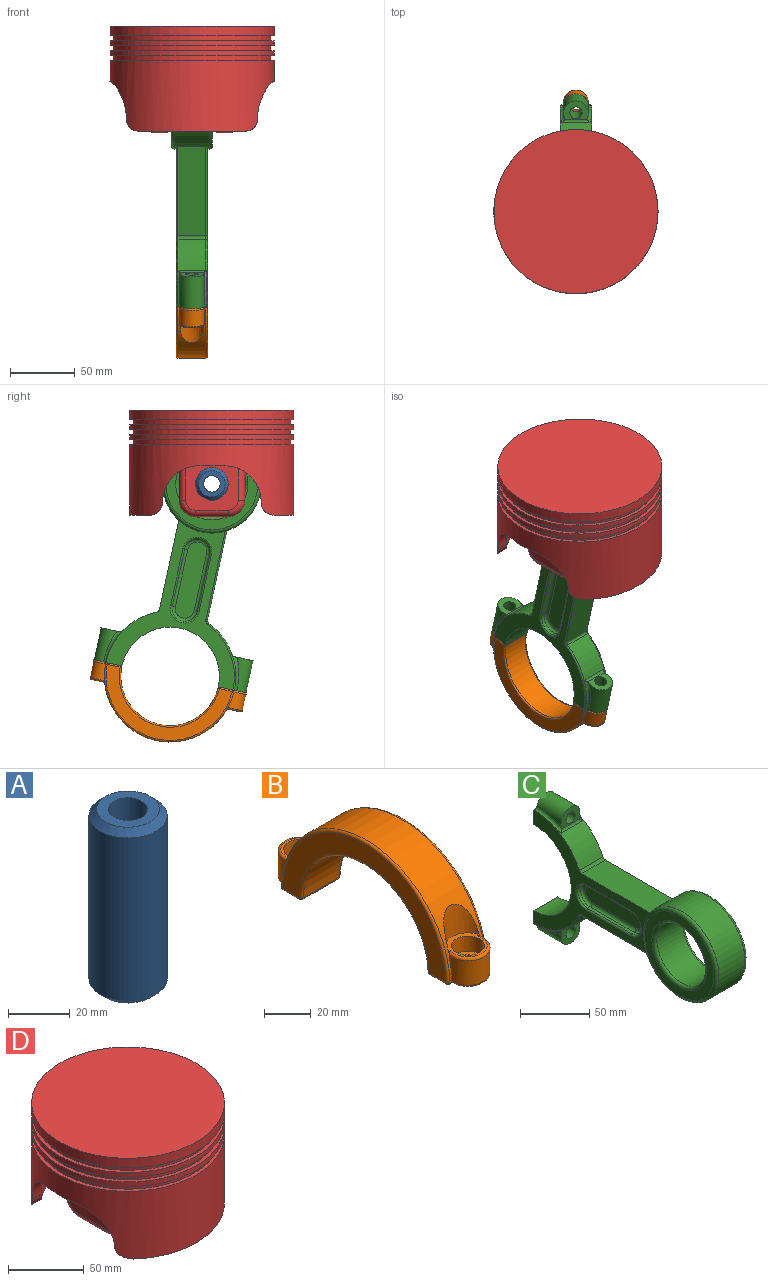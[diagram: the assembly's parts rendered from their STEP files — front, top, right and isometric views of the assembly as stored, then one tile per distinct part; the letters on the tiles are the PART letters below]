
ASSEMBLY  parts=4 mates=5
PART A: 6 faces, bbox 25.4x25.4x69.9 mm
  f0: cylinder r=6.35mm len=69.85mm, axis (0,0,-1), area 2786.9mm2, adj f2,f3
  f1: cylinder r=12.7mm len=64.85mm, axis (0,0,-1), area 5174.8mm2, adj f4,f5
  f2: plane 20.4x20.4mm, normal (0,0,1), area 200.2mm2, adj f0,f5
  f3: plane 20.4x20.4mm, normal (0,0,-1), area 200.2mm2, adj f0,f4
  f4: cone r=12.7mm half-angle=45deg, axis (0,0,1), area 254.4mm2, adj f1,f3
  f5: cone r=10.2mm half-angle=45deg, axis (0,0,-1), area 254.4mm2, adj f1,f2
PART B: 46 faces, bbox 24.1x122.2x55 mm
  f0: cylinder r=50.8mm len=101.57mm, axis (-1,0,0), area 2320.8mm2, adj f6,f7,f8,f12,f13,f14,f21,f29
  f1: plane 21.63x19.75mm, normal (0,0,-1), area 245.3mm2, adj f20,f21,f22,f25,f30,f31,f44
  f2: cylinder r=38.1mm len=76.16mm, axis (-1,0,0), area 2536.6mm2, adj f22,f23,f32,f33
  f3: plane 21.63x19.75mm, normal (0,0,-1), area 245.3mm2, adj f18,f28,f33,f37,f39,f40,f42
  f4: plane 99.07x48.3mm, normal (1,0,0), area 1398.9mm2, adj f20,f23,f28,f29
  f5: plane 99.07x48.3mm, normal (-1,0,0), area 1398.9mm2, adj f31,f32,f38,f39
  f6: plane 18.46x17.8mm, normal (0,0,1), area 84.7mm2, adj f0,f8,f11,f45
  f7: cylinder r=9.53mm len=19.05mm, axis (0,0,-1), area 399.8mm2, adj f0,f21,f25,f30,f45
  f8: cone r=9.53mm half-angle=4deg, axis (0,0,1), area 290.7mm2, adj f0,f6
  f9: cylinder r=4.5mm len=9mm, axis (0,0,1), area 169.6mm2, adj f10,f44
  f10: plane 14.25x14.25mm, normal (0,0,1), area 95.9mm2, adj f9,f11
  f11: cylinder r=7.12mm len=14.25mm, axis (0,0,1), area 358.1mm2, adj f6,f10
  f12: plane 18.46x17.8mm, normal (0,0,1), area 84.7mm2, adj f0,f14,f17,f43
  f13: cylinder r=9.53mm len=19.05mm, axis (0,0,-1), area 399.8mm2, adj f0,f37,f40,f42,f43
  f14: cone r=9.53mm half-angle=4deg, axis (0,0,1), area 290.7mm2, adj f0,f12
  f15: cylinder r=4.5mm len=9mm, axis (0,0,1), area 169.6mm2, adj f16,f18
  f16: plane 14.25x14.25mm, normal (0,0,1), area 95.9mm2, adj f15,f17
  f17: cylinder r=7.12mm len=14.25mm, axis (0,0,1), area 358.1mm2, adj f12,f16
  f18: torus R=5.75mm, axis (0,0,1), area 61.1mm2, adj f3,f15
  f19: sphere r=1.25mm, area 2.4mm2, adj f20,f22,f23
  f20: cylinder r=1.25mm len=10.2mm, axis (0,-1,0), area 20mm2, adj f1,f4,f19,f24
  f21: cylinder r=1.25mm len=2.64mm, axis (-1,0,0), area 3.5mm2, adj f0,f1,f7,f24,f25
  f22: cylinder r=1.25mm len=21.63mm, axis (-1,0,0), area 41.6mm2, adj f1,f2,f19,f26
  f23: torus R=39.35mm, axis (1,0,0), area 233mm2, adj f2,f4,f19,f27
  f24: sphere r=1.25mm, area 2.5mm2, adj f20,f21,f29
  f25: torus R=8.27mm, axis (0,0,1), area 57.8mm2, adj f1,f7,f21,f30
  f26: sphere r=1.25mm, area 2.4mm2, adj f22,f31,f32
  f27: sphere r=1.25mm, area 2.4mm2, adj f23,f28,f33
  f28: cylinder r=1.25mm len=10.2mm, axis (0,-1,0), area 20mm2, adj f3,f4,f27,f34
  f29: torus R=49.55mm, axis (1,0,0), area 305.6mm2, adj f0,f4,f24,f34
  f30: cylinder r=1.25mm len=2.64mm, axis (-1,0,0), area 3.5mm2, adj f0,f1,f7,f25,f35
  f31: cylinder r=1.25mm len=10.2mm, axis (0,1,0), area 20mm2, adj f1,f5,f26,f35
  f32: torus R=39.35mm, axis (1,0,0), area 233mm2, adj f2,f5,f26,f36
  f33: cylinder r=1.25mm len=21.63mm, axis (-1,0,0), area 41.6mm2, adj f2,f3,f27,f36
  f34: sphere r=1.25mm, area 2.5mm2, adj f28,f29,f37
  f35: sphere r=1.25mm, area 2.5mm2, adj f30,f31,f38
  f36: sphere r=1.25mm, area 2.4mm2, adj f32,f33,f39
  f37: cylinder r=1.25mm len=2.64mm, axis (-1,0,0), area 3.5mm2, adj f0,f3,f13,f34,f40
  f38: torus R=49.55mm, axis (1,0,0), area 305.6mm2, adj f0,f5,f35,f41
  f39: cylinder r=1.25mm len=10.2mm, axis (0,1,0), area 20mm2, adj f3,f5,f36,f41
  f40: torus R=8.27mm, axis (0,0,1), area 57.8mm2, adj f3,f13,f37,f42
  f41: sphere r=1.25mm, area 2.5mm2, adj f38,f39,f42
  f42: cylinder r=1.25mm len=2.64mm, axis (-1,0,0), area 3.5mm2, adj f0,f3,f13,f40,f41
  f43: torus R=8.27mm, axis (0,0,-1), area 64.7mm2, adj f0,f12,f13
  f44: torus R=5.75mm, axis (0,0,1), area 61.1mm2, adj f1,f9
  f45: torus R=8.27mm, axis (0,0,-1), area 64.7mm2, adj f0,f6,f7
PART C: 68 faces, bbox 31.9x199x120.8 mm
  f0: cylinder r=50.8mm len=22.73mm, axis (-1,0,0), area 662.3mm2, adj f42,f43,f44,f51,f54,f57
  f1: cylinder r=50.8mm len=15.49mm, axis (-1,0,0), area 2.1mm2, adj f7,f10,f41
  f2: cylinder r=50.8mm len=30.96mm, axis (-1,0,0), area 754.3mm2, adj f9,f10,f39,f40,f41,f49
  f3: cylinder r=50.8mm len=15.49mm, axis (-1,0,0), area 2.1mm2, adj f7,f9,f39
  f4: plane 70.63x21.63mm, normal (0,0,-1), area 1527.7mm2, adj f11,f51,f52,f59
  f5: plane 24.15x22.25mm, normal (0,1,0), area 379.3mm2, adj f6,f9,f10,f16,f17,f42,f43,f55
  f6: cylinder r=38.1mm len=76.2mm, axis (-1,0,0), area 2888.2mm2, adj f5,f7,f9,f10
  f7: plane 24.18x22.28mm, normal (0,1,0), area 379.7mm2, adj f1,f3,f6,f9,f10,f18,f20,f39
  f8: plane 69.19x24.13mm, normal (0,0,1), area 1669.6mm2, adj f9,f10,f49,f50
  f9: plane 120.13x100.48mm, normal (1,0,0), area 2732.6mm2, adj f2,f3,f5,f6,f7,f8,f11,f49
  f10: plane 120.13x100.48mm, normal (-1,0,0), area 2732.6mm2, adj f1,f2,f5,f6,f7,f8,f11,f49
  f11: cylinder r=38.1mm len=76.2mm, axis (-1,0,0), area 5390mm2, adj f4,f9,f10,f46,f48,f50,f52,f59
  f12: cylinder r=25.4mm len=50.8mm, axis (-1,0,0), area 4256.3mm2, adj f45,f47
  f13: plane 71.12x71.12mm, normal (1,0,0), area 1520.1mm2, adj f47,f48
  f14: plane 71.12x71.12mm, normal (-1,0,0), area 1520.1mm2, adj f45,f46
  f15: plane 19.05x14.89mm, normal (0,-1,0), area 169.6mm2, adj f16,f17,f42,f43,f44
  f16: cylinder r=9.53mm len=25.4mm, axis (0,1,0), area 788.3mm2, adj f5,f15,f42,f43
  f17: cylinder r=4.76mm len=25.4mm, axis (0,1,0), area 759.7mm2, adj f5,f15
  f18: cylinder r=9.53mm len=25.4mm, axis (0,1,0), area 788.3mm2, adj f7,f19,f39,f41
  f19: plane 19.17x15.01mm, normal (0,-1,0), area 169.6mm2, adj f18,f20,f39,f40,f41
  f20: cylinder r=4.76mm len=25.4mm, axis (0,1,0), area 759.7mm2, adj f7,f19
  f21: plane 45x2.56mm, normal (0,0,1), area 115.2mm2, adj f22,f24,f35,f64
  f22: cylinder r=10mm len=20mm, axis (1,0,0), area 80.4mm2, adj f21,f23,f36,f65
  f23: plane 45x2.56mm, normal (0,0,-1), area 115.2mm2, adj f22,f24,f38,f67
  f24: cylinder r=10mm len=20mm, axis (1,0,0), area 80.4mm2, adj f21,f23,f37,f66
  f25: plane 59.92x14.92mm, normal (1,0,0), area 846.2mm2, adj f35,f36,f37,f38
  f26: plane 45x2.56mm, normal (0,0,1), area 115.2mm2, adj f27,f29,f31,f63
  f27: cylinder r=10mm len=20mm, axis (-1,0,0), area 80.4mm2, adj f26,f28,f33,f62
  f28: plane 45x2.56mm, normal (0,0,-1), area 115.2mm2, adj f27,f29,f34,f60
  f29: cylinder r=10mm len=20mm, axis (-1,0,0), area 80.4mm2, adj f26,f28,f32,f61
  f30: plane 59.92x14.92mm, normal (-1,0,0), area 846.2mm2, adj f31,f32,f33,f34
  f31: cylinder r=2.54mm len=45mm, axis (0,-1,0), area 179.5mm2, adj f26,f30,f32,f33
  f32: torus R=7.46mm, axis (-1,0,0), area 113.8mm2, adj f29,f30,f31,f34
  f33: torus R=7.46mm, axis (-1,0,0), area 113.8mm2, adj f27,f30,f31,f34
  f34: cylinder r=2.54mm len=45mm, axis (0,1,0), area 179.5mm2, adj f28,f30,f32,f33
  f35: cylinder r=2.54mm len=45mm, axis (0,1,0), area 179.5mm2, adj f21,f25,f36,f37
  f36: torus R=7.46mm, axis (1,0,0), area 113.8mm2, adj f22,f25,f35,f38
  f37: torus R=7.46mm, axis (1,0,0), area 113.8mm2, adj f24,f25,f35,f38
  f38: cylinder r=2.54mm len=45mm, axis (0,-1,0), area 179.5mm2, adj f23,f25,f36,f37
  f39: bspline ~33.55x11.07mm, area 105.2mm2, adj f2,f3,f7,f18,f19,f40
  f40: cylinder r=2.54mm len=21.62mm, axis (-1,0,0), area 51.5mm2, adj f2,f19,f39,f41
  f41: bspline ~31.85x10.39mm, area 105.2mm2, adj f1,f2,f7,f18,f19,f40
  f42: bspline ~32.45x10.36mm, area 85.8mm2, adj f0,f5,f15,f16,f44,f56
  f43: bspline ~31.54x10.2mm, area 85.8mm2, adj f0,f5,f15,f16,f44,f55
  f44: cylinder r=2.54mm len=21.62mm, axis (-1,0,0), area 51.5mm2, adj f0,f15,f42,f43
  f45: torus R=27.94mm, axis (1,0,0), area 659.9mm2, adj f12,f14
  f46: torus R=35.56mm, axis (1,0,0), area 932mm2, adj f11,f14
  f47: torus R=27.94mm, axis (1,0,0), area 659.9mm2, adj f12,f13
  f48: torus R=35.56mm, axis (1,0,0), area 932mm2, adj f11,f13
  f49: cylinder r=2.54mm len=24.13mm, axis (-1,0,0), area 70.7mm2, adj f2,f8,f9,f10
  f50: cylinder r=2.54mm len=24.13mm, axis (-1,0,0), area 61.9mm2, adj f8,f9,f10,f11
  f51: cylinder r=2.54mm len=21.63mm, axis (-1,0,0), area 63.4mm2, adj f0,f4,f53,f58
  f52: cylinder r=1.25mm len=70.63mm, axis (0,1,0), area 138mm2, adj f4,f10,f11,f53
  f53: torus R=3.79mm, axis (1,0,0), area 6.8mm2, adj f10,f51,f52,f54
  f54: torus R=49.55mm, axis (1,0,0), area 59.6mm2, adj f0,f10,f53,f55
  f55: bspline ~32.87x9.3mm, area 45.1mm2, adj f5,f10,f43,f54
  f56: bspline ~31.09x9.09mm, area 45.1mm2, adj f5,f9,f42,f57
  f57: torus R=49.55mm, axis (1,0,0), area 59.6mm2, adj f0,f9,f56,f58
  f58: torus R=3.79mm, axis (1,0,0), area 6.8mm2, adj f9,f51,f57,f59
  f59: cylinder r=1.25mm len=70.63mm, axis (0,-1,0), area 138mm2, adj f4,f9,f11,f58
  f60: cylinder r=1.25mm len=45mm, axis (0,1,0), area 88.4mm2, adj f10,f28,f61,f62
  f61: torus R=11.25mm, axis (1,0,0), area 64.5mm2, adj f10,f29,f60,f63
  f62: torus R=11.25mm, axis (1,0,0), area 64.5mm2, adj f10,f27,f60,f63
  f63: cylinder r=1.25mm len=45mm, axis (0,-1,0), area 88.4mm2, adj f10,f26,f61,f62
  f64: cylinder r=1.25mm len=45mm, axis (0,-1,0), area 88.4mm2, adj f9,f21,f65,f66
  f65: torus R=11.25mm, axis (1,0,0), area 64.5mm2, adj f9,f22,f64,f67
  f66: torus R=11.25mm, axis (1,0,0), area 64.5mm2, adj f9,f24,f64,f67
  f67: cylinder r=1.25mm len=45mm, axis (0,1,0), area 88.4mm2, adj f9,f23,f65,f66
PART D: 68 faces, bbox 127x127x83.5 mm
  f0: plane 114.3x114.3mm, normal (0,0,-1), area 8373.3mm2, adj f12,f28,f29,f30,f31,f33,f34,f35
  f1: plane 82.91x15.4mm, normal (0,0,-1), area 495.6mm2, adj f10,f12,f44,f46
  f2: cylinder r=63.5mm len=127mm, axis (0,0,1), area 1520.1mm2, adj f6,f7
  f3: cylinder r=63.5mm len=127mm, axis (0,0,1), area 1520.1mm2, adj f9,f13
  f4: plane 127x127mm, normal (0,0,1), area 993.1mm2, adj f5,f10
  f5: cylinder r=60.96mm len=121.92mm, axis (0,0,1), area 1459.3mm2, adj f4,f6
  f6: plane 127x127mm, normal (0,0,-1), area 993.1mm2, adj f2,f5
  f7: plane 127x127mm, normal (0,0,1), area 993.1mm2, adj f2,f8
  f8: cylinder r=60.96mm len=121.92mm, axis (0,0,1), area 1459.3mm2, adj f7,f9
  f9: plane 127x127mm, normal (0,0,-1), area 993.1mm2, adj f3,f8
  f10: cylinder r=63.5mm len=127mm, axis (0,0,1), area 16234.2mm2, adj f1,f4,f11,f18,f19,f20,f21,f22
  f11: plane 82.91x15.4mm, normal (0,0,-1), area 495.6mm2, adj f10,f12,f45,f47
  f12: cylinder r=57.15mm len=114.3mm, axis (0,0,-1), area 16707.7mm2, adj f0,f1,f11,f18,f19,f20,f21,f22
  f13: plane 127x127mm, normal (0,0,1), area 993.1mm2, adj f3,f14
  f14: cylinder r=60.96mm len=121.92mm, axis (0,0,1), area 1459.3mm2, adj f13,f15
  f15: plane 127x127mm, normal (0,0,-1), area 993.1mm2, adj f14,f17
  f16: plane 127x127mm, normal (0,0,1), area 12667.7mm2, adj f17
  f17: cylinder r=63.5mm len=127mm, axis (0,0,1), area 3040.2mm2, adj f15,f16
  f18: plane 8.2x0.1mm, normal (0,1,0), area 0.8mm2, adj f10,f12,f27,f47
  f19: plane 20.2x7.25mm, normal (0,0,-1), area 128.9mm2, adj f10,f12,f26,f27
  f20: plane 8.2x0.1mm, normal (0,-1,0), area 0.8mm2, adj f10,f12,f26,f46
  f21: plane 8.2x0.1mm, normal (0,-1,0), area 0.8mm2, adj f10,f12,f24,f44
  f22: plane 20.2x7.25mm, normal (0,0,-1), area 128.9mm2, adj f10,f12,f24,f25
  f23: plane 8.2x0.1mm, normal (0,1,0), area 0.8mm2, adj f10,f12,f25,f45
  f24: cylinder r=28mm len=28mm, axis (-1,0,0), area 322.6mm2, adj f10,f12,f21,f22
  f25: cylinder r=28mm len=28mm, axis (1,0,0), area 322.6mm2, adj f10,f12,f22,f23
  f26: cylinder r=28mm len=28mm, axis (-1,0,0), area 322.6mm2, adj f10,f12,f19,f20
  f27: cylinder r=28mm len=28mm, axis (1,0,0), area 322.6mm2, adj f10,f12,f18,f19
  f28: plane 58.5x40.8mm, normal (-1,0,0), area 1854.6mm2, adj f0,f39,f53,f54,f55,f56,f57
  f29: plane 50.8x9mm, normal (0,1,0), area 457.2mm2, adj f0,f42,f52,f57
  f30: plane 58.5x40.8mm, normal (1,0,0), area 1854.6mm2, adj f0,f39,f48,f49,f50,f51,f52
  f31: plane 50.8x9mm, normal (0,-1,0), area 457.2mm2, adj f0,f43,f48,f53
  f32: plane 25.4x9mm, normal (0,0,-1), area 228.6mm2, adj f42,f43,f50,f55
  f33: plane 58.5x40.8mm, normal (1,0,0), area 1854.6mm2, adj f0,f38,f63,f64,f65,f66,f67
  f34: plane 50.8x9mm, normal (0,-1,0), area 457.2mm2, adj f0,f40,f58,f63
  f35: plane 58.5x40.8mm, normal (-1,0,0), area 1854.6mm2, adj f0,f38,f58,f59,f60,f61,f62
  f36: plane 50.8x9mm, normal (0,1,0), area 457.2mm2, adj f0,f41,f62,f67
  f37: plane 25.4x9mm, normal (0,0,-1), area 228.6mm2, adj f40,f41,f60,f65
  f38: cylinder r=12.7mm len=25.4mm, axis (1,0,0), area 1516.1mm2, adj f33,f35
  f39: cylinder r=12.7mm len=25.4mm, axis (1,0,0), area 1516.1mm2, adj f28,f30
  f40: cylinder r=12.7mm len=12.7mm, axis (1,0,0), area 179.5mm2, adj f34,f37,f59,f64
  f41: cylinder r=12.7mm len=12.7mm, axis (-1,0,0), area 179.5mm2, adj f36,f37,f61,f66
  f42: cylinder r=12.7mm len=12.7mm, axis (-1,0,0), area 179.5mm2, adj f29,f32,f51,f56
  f43: cylinder r=12.7mm len=12.7mm, axis (1,0,0), area 179.5mm2, adj f31,f32,f49,f54
  f44: cylinder r=10mm len=19.94mm, axis (1,0,0), area 140mm2, adj f1,f10,f12,f21
  f45: cylinder r=10mm len=19.94mm, axis (-1,0,0), area 140mm2, adj f10,f11,f12,f23
  f46: cylinder r=10mm len=19.94mm, axis (1,0,0), area 140mm2, adj f1,f10,f12,f20
  f47: cylinder r=10mm len=19.94mm, axis (-1,0,0), area 140mm2, adj f10,f11,f12,f18
  f48: cylinder r=5mm len=50.8mm, axis (0,0,-1), area 399mm2, adj f0,f30,f31,f49
  f49: torus R=7.7mm, axis (-1,0,0), area 134.3mm2, adj f30,f43,f48,f50
  f50: cylinder r=5mm len=25.4mm, axis (0,1,0), area 199.5mm2, adj f30,f32,f49,f51
  f51: torus R=7.7mm, axis (-1,0,0), area 134.3mm2, adj f30,f42,f50,f52
  f52: cylinder r=5mm len=50.8mm, axis (0,0,1), area 399mm2, adj f0,f29,f30,f51
  f53: cylinder r=5mm len=50.8mm, axis (0,0,1), area 399mm2, adj f0,f28,f31,f54
  f54: torus R=7.7mm, axis (-1,0,0), area 134.3mm2, adj f28,f43,f53,f55
  f55: cylinder r=5mm len=25.4mm, axis (0,-1,0), area 199.5mm2, adj f28,f32,f54,f56
  f56: torus R=7.7mm, axis (-1,0,0), area 134.3mm2, adj f28,f42,f55,f57
  f57: cylinder r=5mm len=50.8mm, axis (0,0,-1), area 399mm2, adj f0,f28,f29,f56
  f58: cylinder r=5mm len=50.8mm, axis (0,0,-1), area 399mm2, adj f0,f34,f35,f59
  f59: torus R=7.7mm, axis (-1,0,0), area 134.3mm2, adj f35,f40,f58,f60
  f60: cylinder r=5mm len=25.4mm, axis (0,-1,0), area 199.5mm2, adj f35,f37,f59,f61
  f61: torus R=7.7mm, axis (-1,0,0), area 134.3mm2, adj f35,f41,f60,f62
  f62: cylinder r=5mm len=50.8mm, axis (0,0,1), area 399mm2, adj f0,f35,f36,f61
  f63: cylinder r=5mm len=50.8mm, axis (0,0,1), area 399mm2, adj f0,f33,f34,f64
  f64: torus R=7.7mm, axis (-1,0,0), area 134.3mm2, adj f33,f40,f63,f65
  f65: cylinder r=5mm len=25.4mm, axis (0,1,0), area 199.5mm2, adj f33,f37,f64,f66
  f66: torus R=7.7mm, axis (-1,0,0), area 134.3mm2, adj f33,f41,f65,f67
  f67: cylinder r=5mm len=50.8mm, axis (0,0,-1), area 399mm2, adj f0,f33,f36,f66
PLACE A rot(axis=(-0.53,-0.66,0.53),113.5deg) t=(-82.99,-134.76,60.3)mm
PLACE B rot(axis=(-1,0,0),167.8deg) t=(-82.94,-102.43,-88.63)mm
PLACE C rot(axis=(-1,0,0),77.8deg) t=(-82.94,-118.59,-14.17)mm
PLACE D t=(-82.94,-134.76,117.4)mm fixed
MATE pin_slot A.f1 <-> D.f38  axis (1,0,0) through (-48.06,-134.76,60.3)mm
MATE planar D.f41 <-> C.f11  axis (-1,0,0) through (-67.06,-122.06,47.6)mm
MATE fastened B.f13 <-> C.f16  axis (0,-0.21,0.98) through (-82.94,-152.07,-99.41)mm
MATE cylindrical C.f11 <-> A.f1  axis (-1,0,0) through (-69.6,-134.76,60.3)mm
MATE cylindrical A.f0 <-> D.f38  axis (1,0,0) through (-48.06,-134.76,60.3)mm
